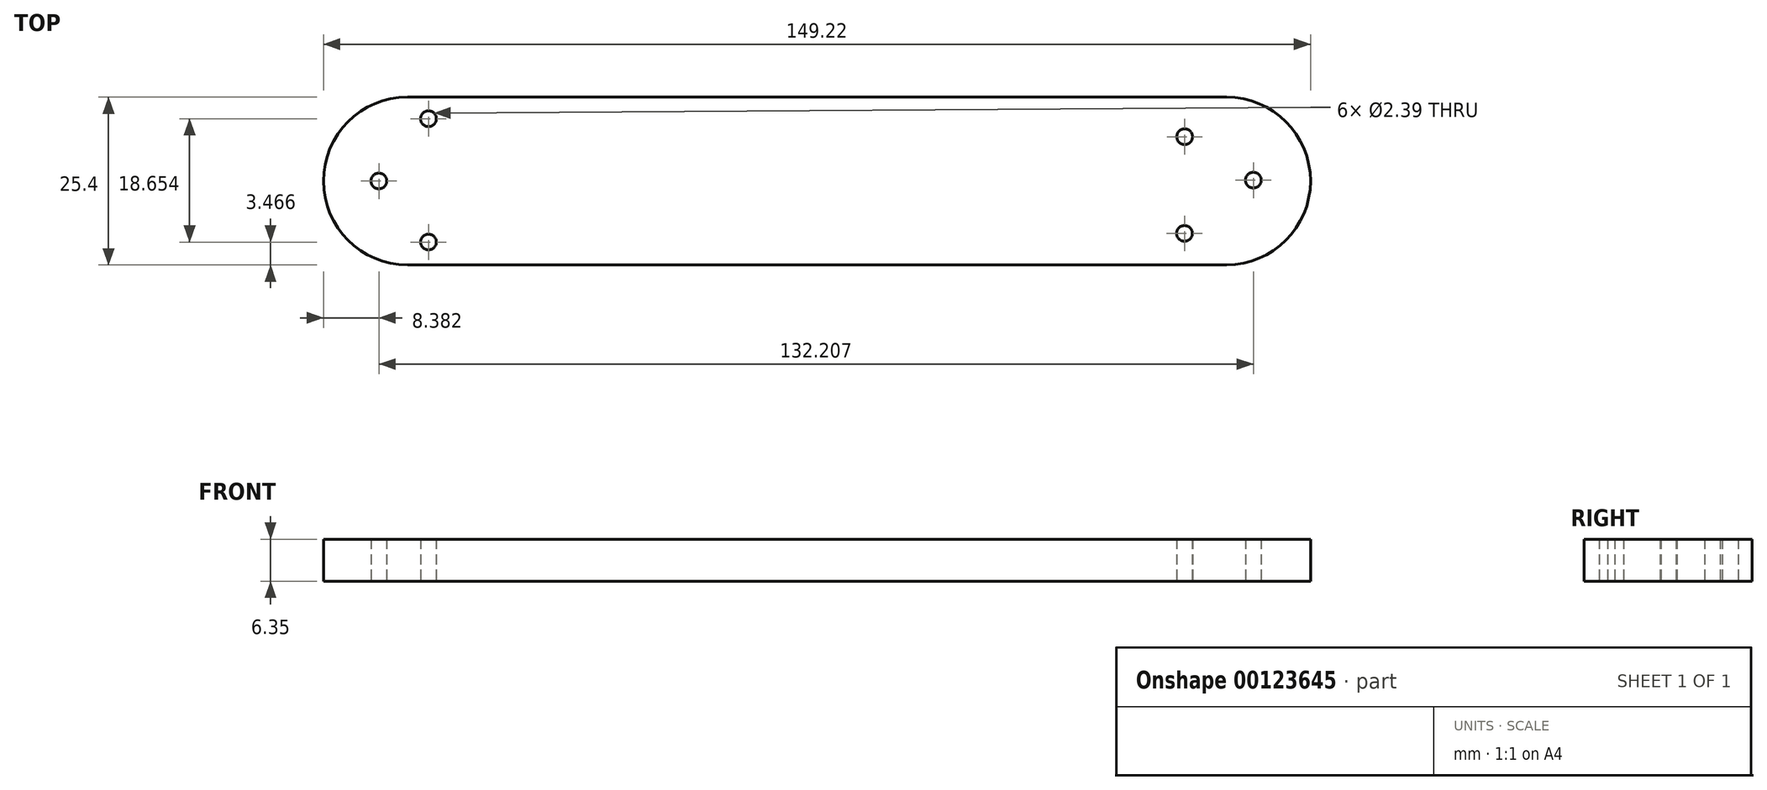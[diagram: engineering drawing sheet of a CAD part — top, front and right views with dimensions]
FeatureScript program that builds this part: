
annotation { "Feature Type Name" : "Feature", "Feature Type Description" : "" }
export const myFeature = defineFeature(function(context is Context, id is Id, definition is map)
    precondition{}
    {
        {
            var Q0;
            Q0=qCreatedBy(makeId("Top.planeOp"),FACE);
            var sketch = newSketch(context, id + "F0", { "sketchPlane" : qUnion([Q0])});
            skPoint(sketch, "E0", {"position": v(8.38, 0) * mm});
            skPoint(sketch, "E1", {"position": v(3.48, 0) * mm});
            skPoint(sketch, "E2", {"position": v(8.38, -12.9) * mm});
            skCircle(sketch, "E3", {"center": v(8.38, -12.9) * mm, "radius": 1.2 * mm});
            skPoint(sketch, "E4", {"position": v(0, -3.48) * mm});
            skPoint(sketch, "E5", {"position": v(8.38, -3.48) * mm});
            skPoint(sketch, "E6", {"position": v(8.38, -22) * mm});
            skPoint(sketch, "E7", {"position": v(15.88, 0) * mm});
            skLineSegment(sketch, "E8", {"start": v(15.88, 0) * mm, "end": v(15.88, -0.32) * mm});
            skPoint(sketch, "E9", {"position": v(15.88, -3.48) * mm});
            skPoint(sketch, "E10", {"position": v(15.88, -22.13) * mm});
            skCircle(sketch, "E11", {"center": v(15.88, -3.48) * mm, "radius": 1.2 * mm});
            skCircle(sketch, "E12", {"center": v(15.88, -22.13) * mm, "radius": 1.2 * mm});
            skPoint(sketch, "E13", {"position": v(140.59, 0) * mm});
            skLineSegment(sketch, "E14", {"start": v(140.59, 0) * mm, "end": v(140.59, -0.86) * mm});
            skCircle(sketch, "E15", {"center": v(140.59, -12.77) * mm, "radius": 1.2 * mm});
            skPoint(sketch, "E16", {"position": v(12.7, -12.9) * mm});
            skArc(sketch, "E17", {"start": v(136.53, -25.6) * mm, "mid": v(149.22, -12.9) * mm, "end": v(136.53, -0.2) * mm});
            skPoint(sketch, "E18", {"position": v(66.24, -0.27) * mm});
            skPoint(sketch, "E19.orphan", {"position": v(0, -12.9) * mm});
            skPoint(sketch, "E20", {"position": v(74.63, -25.66) * mm});
            skCircle(sketch, "E21", {"center": v(130.18, -20.83) * mm, "radius": 1.2 * mm});
            skCircle(sketch, "E22", {"center": v(130.2, -6.2) * mm, "radius": 1.2 * mm});
            skArc(sketch, "E23", {"start": v(12.7, -0.2) * mm, "mid": v(0, -12.9) * mm, "end": v(12.7, -25.6) * mm});
            skLineSegment(sketch, "E24.top", {"start": v(12.7, -25.6) * mm, "end": v(136.53, -25.6) * mm});
            skLineSegment(sketch, "E25.top", {"start": v(12.7, -0.2) * mm, "end": v(136.53, -0.2) * mm});
            skCircle(sketch, "E26", {"center": v(15.88, -3.48) * mm, "radius": 2.38 * mm});
            skCircle(sketch, "E27", {"center": v(15.88, -22.13) * mm, "radius": 2.13 * mm});
            skCircle(sketch, "E28", {"center": v(130.2, -6.2) * mm, "radius": 4.86 * mm});
            skCircle(sketch, "E29", {"center": v(130.18, -20.83) * mm, "radius": 2.84 * mm});
            skCircle(sketch, "E30", {"center": v(8.38, -12.9) * mm, "radius": 6.6 * mm});
            skCircle(sketch, "E31", {"center": v(140.59, -12.77) * mm, "radius": 3.43 * mm});
            skSolve(sketch);
        }
        {
            var Q0;
            {var subQ0=sQuery(id+"F0.wireOp",EDGE,"E23");Q0=makeQuery(id+"F0.imprint","IMPRINT",FACE,{"disambiguationData":[TD([[makeQuery(id+"F0.imprint","IMPRINT",EDGE,{"derivedFrom":subQ0}),1.0]])]});}
            var Q1;
            Q1=makeQuery(id+"F0.imprint","IMPRINT",FACE,{"disambiguationData":[TD([[makeQuery(id+"F0.imprint","IMPRINT",EDGE,{"derivedFrom":sQuery(id+"F0.wireOp",EDGE,"E3")}),-1.0]])]});
            var Q2;
            Q2=makeQuery(id+"F0.imprint","IMPRINT",FACE,{"disambiguationData":[TD([[makeQuery(id+"F0.imprint","IMPRINT",EDGE,{"derivedFrom":sQuery(id+"F0.wireOp",EDGE,"E12")}),-1.0]])]});
            var Q3;
            Q3=makeQuery(id+"F0.imprint","IMPRINT",FACE,{"disambiguationData":[TD([[makeQuery(id+"F0.imprint","IMPRINT",EDGE,{"derivedFrom":sQuery(id+"F0.wireOp",EDGE,"E11")}),-1.0]])]});
            var Q4;
            Q4=makeQuery(id+"F0.imprint","IMPRINT",FACE,{"disambiguationData":[TD([[makeQuery(id+"F0.imprint","IMPRINT",EDGE,{"derivedFrom":sQuery(id+"F0.wireOp",EDGE,"E22")}),-1.0]])]});
            var Q5;
            Q5=makeQuery(id+"F0.imprint","IMPRINT",FACE,{"disambiguationData":[TD([[makeQuery(id+"F0.imprint","IMPRINT",EDGE,{"derivedFrom":sQuery(id+"F0.wireOp",EDGE,"E15")}),-1.0]])]});
            var Q6;
            Q6=makeQuery(id+"F0.imprint","IMPRINT",FACE,{"disambiguationData":[TD([[makeQuery(id+"F0.imprint","IMPRINT",EDGE,{"derivedFrom":sQuery(id+"F0.wireOp",EDGE,"E21")}),-1.0]])]});
            extrude(context, id + "F1", {"entities" : qUnion([Q0, Q1, Q2, Q3, Q4, Q5, Q6]), "depth" : 6.35 * mm});
        }
    });
